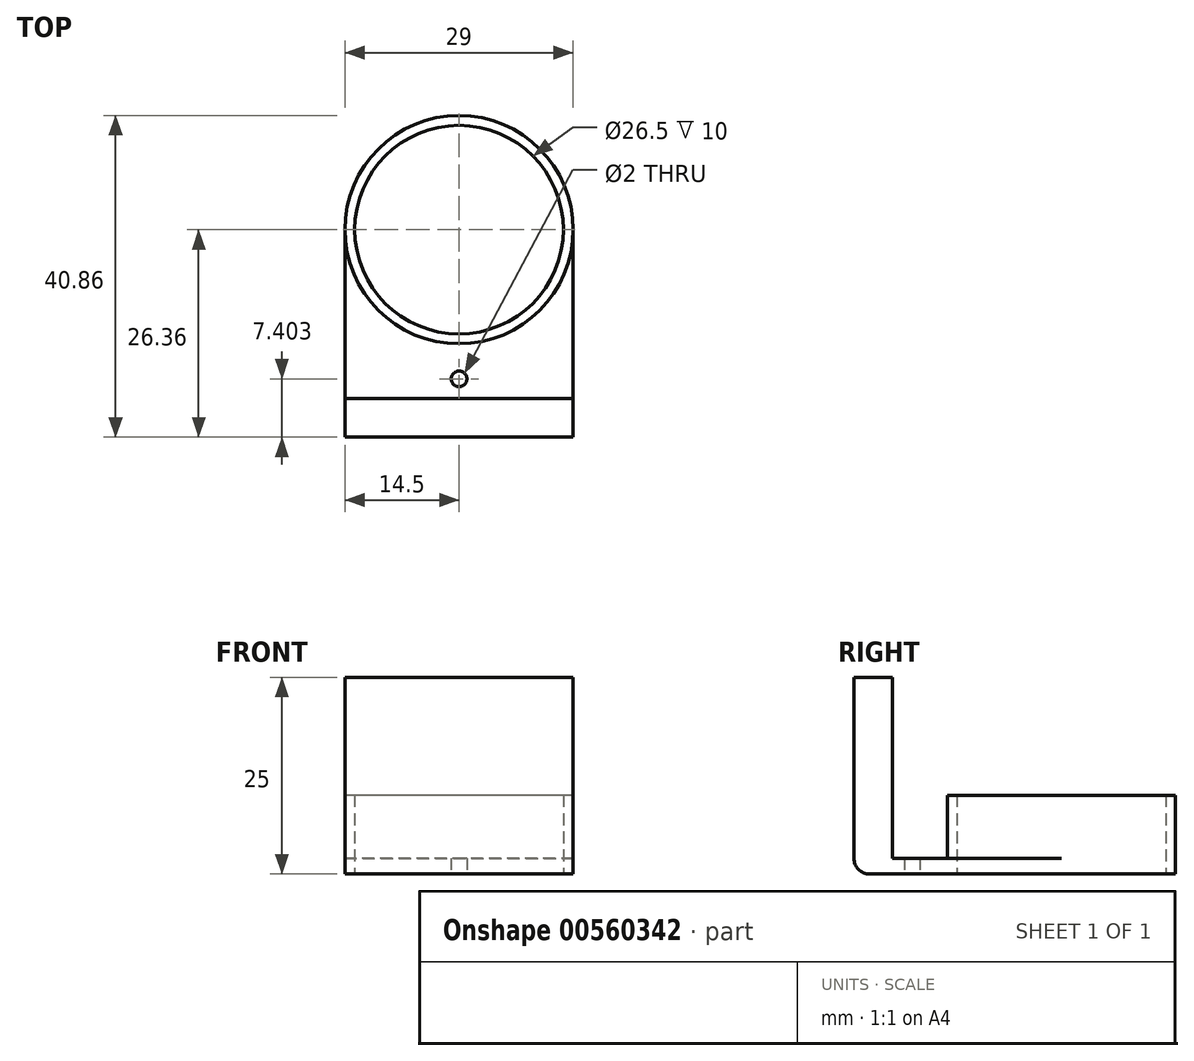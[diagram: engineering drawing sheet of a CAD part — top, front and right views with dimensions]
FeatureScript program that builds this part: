
annotation { "Feature Type Name" : "Feature", "Feature Type Description" : "" }
export const myFeature = defineFeature(function(context is Context, id is Id, definition is map)
    precondition{}
    {
        {
            var Q0;
            Q0=qCreatedBy(makeId("Top.planeOp"),FACE);
            var sketch = newSketch(context, id + "F0", { "sketchPlane" : qUnion([Q0])});
            skCircle(sketch, "E0", {"center": v(0, 0) * mm, "radius": 13.25 * mm});
            skCircle(sketch, "E1", {"center": v(0, 0) * mm, "radius": 14.5 * mm});
            skLineSegment(sketch, "E2", {"start": v(-14.5, 0) * mm, "end": v(-14.5, -21.46) * mm});
            skLineSegment(sketch, "E3", {"start": v(-14.5, -21.46) * mm, "end": v(14.5, -21.46) * mm});
            skLineSegment(sketch, "E4", {"start": v(14.5, -21.46) * mm, "end": v(14.5, 0) * mm});
            skLineSegment(sketch, "E5", {"start": v(-14.5, -21.46) * mm, "end": v(-14.5, -26.36) * mm});
            skLineSegment(sketch, "E6", {"start": v(-14.5, -26.36) * mm, "end": v(14.5, -26.36) * mm});
            skLineSegment(sketch, "E7", {"start": v(14.5, -26.36) * mm, "end": v(14.5, -21.46) * mm});
            skCircle(sketch, "E8", {"center": v(0, -18.96) * mm, "radius": 1 * mm});
            skSolve(sketch);
        }
        {
            var Q0;
            Q0=makeQuery(id+"F0.imprint","IMPRINT",FACE,{"disambiguationData":[TD([[makeQuery(id+"F0.imprint","IMPRINT",EDGE,{"derivedFrom":sQuery(id+"F0.wireOp",EDGE,"E0")}),-1.0]])]});
            extrude(context, id + "F1", {"entities" : qUnion([Q0]), "depth" : 10 * mm});
        }
        {
            var Q0;
            {var subQ0=sQuery(id+"F0.wireOp",EDGE,"E2");Q0=makeQuery(id+"F0.imprint","IMPRINT",FACE,{"disambiguationData":[TD([[makeQuery(id+"F0.imprint","IMPRINT",EDGE,{"derivedFrom":subQ0}),1.0]])]});}
            var Q1;
            Q1=makeQuery(id+"F0.imprint","IMPRINT",FACE,{"disambiguationData":[TD([[makeQuery(id+"F0.imprint","IMPRINT",EDGE,{"derivedFrom":sQuery(id+"F0.wireOp",EDGE,"E3")}),-1.0]])]});
            extrude(context, id + "F2", {"entities" : qUnion([Q0, Q1]), "operationType" : NewBodyOperationType.ADD, "depth" : 2 * mm});
        }
        {
            var Q0;
            Q0=makeQuery(id+"F0.imprint","IMPRINT",FACE,{"disambiguationData":[TD([[makeQuery(id+"F0.imprint","IMPRINT",EDGE,{"derivedFrom":sQuery(id+"F0.wireOp",EDGE,"E3")}),-1.0]])]});
            extrude(context, id + "F3", {"entities" : qUnion([Q0]), "operationType" : NewBodyOperationType.ADD, "depth" : 25 * mm});
        }
        {
            var Q0;
            Q0=makeQuery(id+"F2.opExtrude","CAP_EDGE",EDGE,{"disambiguationData":[OSD([sQuery(id+"F0.wireOp",EDGE,"E6")])],"isStart":true});
            fillet(context, id + "F4", {"entities" : qUnion([Q0]), "radius" : 2 * mm, "tangentPropagation" : true, "allowEdgeOverflow" : false});
        }
    });
